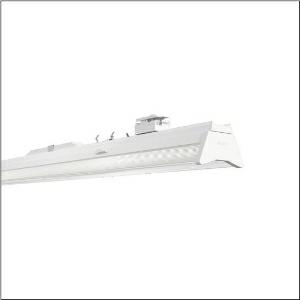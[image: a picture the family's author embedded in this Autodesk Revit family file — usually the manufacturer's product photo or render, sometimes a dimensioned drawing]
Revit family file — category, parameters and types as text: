
# Revit family: licross_r__21_performance_mo_52td16mn4a5g_2767
name_source: partatom
category: Lighting Fixtures
units: mm (PartAtom-declared; Revit-internal decimal feet)

## family parameters
Cut with Voids When Loaded = No
Host = Face
Light Source = No
Part Type = Normal
Room Calculation Point = No
Round Connector Dimension = Use Diameter
Shared = No

## types (1)
- --- (1 x LED, 10890 lm, 60.5 W, 4000K)
    Apparent Load = 61 VA
    CIE Flux Codes = 66 88 96 79 100
    Color Rendering = 80
    Color Temperature = 4000K
    Default Elevation = 1800 mm
    Description = Licross® 21 Performance MO, luminaire insert, of sheet steel, galvanised, coil coated, white, length: 1.500mm, width: 120mm, height: 123mm, LED rated luminous flux: 10.890lm, light colour: 840, control gear: ON/OFF Multilumen, with plug, 3-pole, with phase selection, mains connection: 220..240V, AC, 50/60Hz, rated input power: 61W, internal wiring halogen-free, primary light control with lens, of plastic, primary optical cover: cover, of PMMA, light emission: direct/indirect distribution, primary light characteristic: symmetric, protection rating (complete): IP54, insulation class (complete): insulation class I (protective earthing), certification: CE, ENEC, UKCA, protection symbol: D if used in an environment with non-conductive dust loads with corresponding accessories, impact resistance: IK06, permissible ambient temperature for indoor applications: -35..+45°C, corresponds to IFS (International Featured Standards) requirements for safety and quality in the food industry, reducing of maximum allowable ambient temperature of 5°C with ceiling mounting, LABS conformity tested according to VDMA 24364:2018-05, packaging unit: 1 piece
    Height = 114 mm
    Lamp = 1 x LED
    Lamp Light Flux = 10890 lm
    Lamp Power = 60.5 W
    Lamp count = 1
    Length = 1500 mm
    Luminous efficacy = 180 lm/W
    Manufacturer = Siteco
    ModVariant = No
    Model = 52TD16MN4A5G
    Mounting Place = Ceiling
    Mounting Type = Pendant
    Number of Poles = 1
    OnlyDefault = Yes
    Power Factor = 1
    Product Name = Licross® 21 Performance MO
    Product group = luminaire insert | ceiling pendant
    ProductGroupID = 902
    Protection Class = Protection class I
    Protection Degree = IP 54
    RLX_Detail_Level = 1
    RLX_Emergency_Light_Flux = 0 lm
    RLX_Emergency_Type = 0
    RLX_Emergency_Type_DB = No
    RlxData = <blob elided: 31849 chars, md5=75e27256>
    Socket = socket
    Standby Power = 0 W
    System Light Flux = 10890 lm
    System Power = 61 W
    Type Comments = factory setting: luminous flux: 100 % | (A | C | E) | 140 mA
    Type Image = l_1256138.jpg
    URL = http://relux.com
    VarID = @adj_130657
    Voltage = 0 V
    Weight = 0.00 kg
    Width = 120 mm

## geometry (parser evidence)
native form markers: Blend x4, Sweep x10
no freeform markers — native parametric forms only
